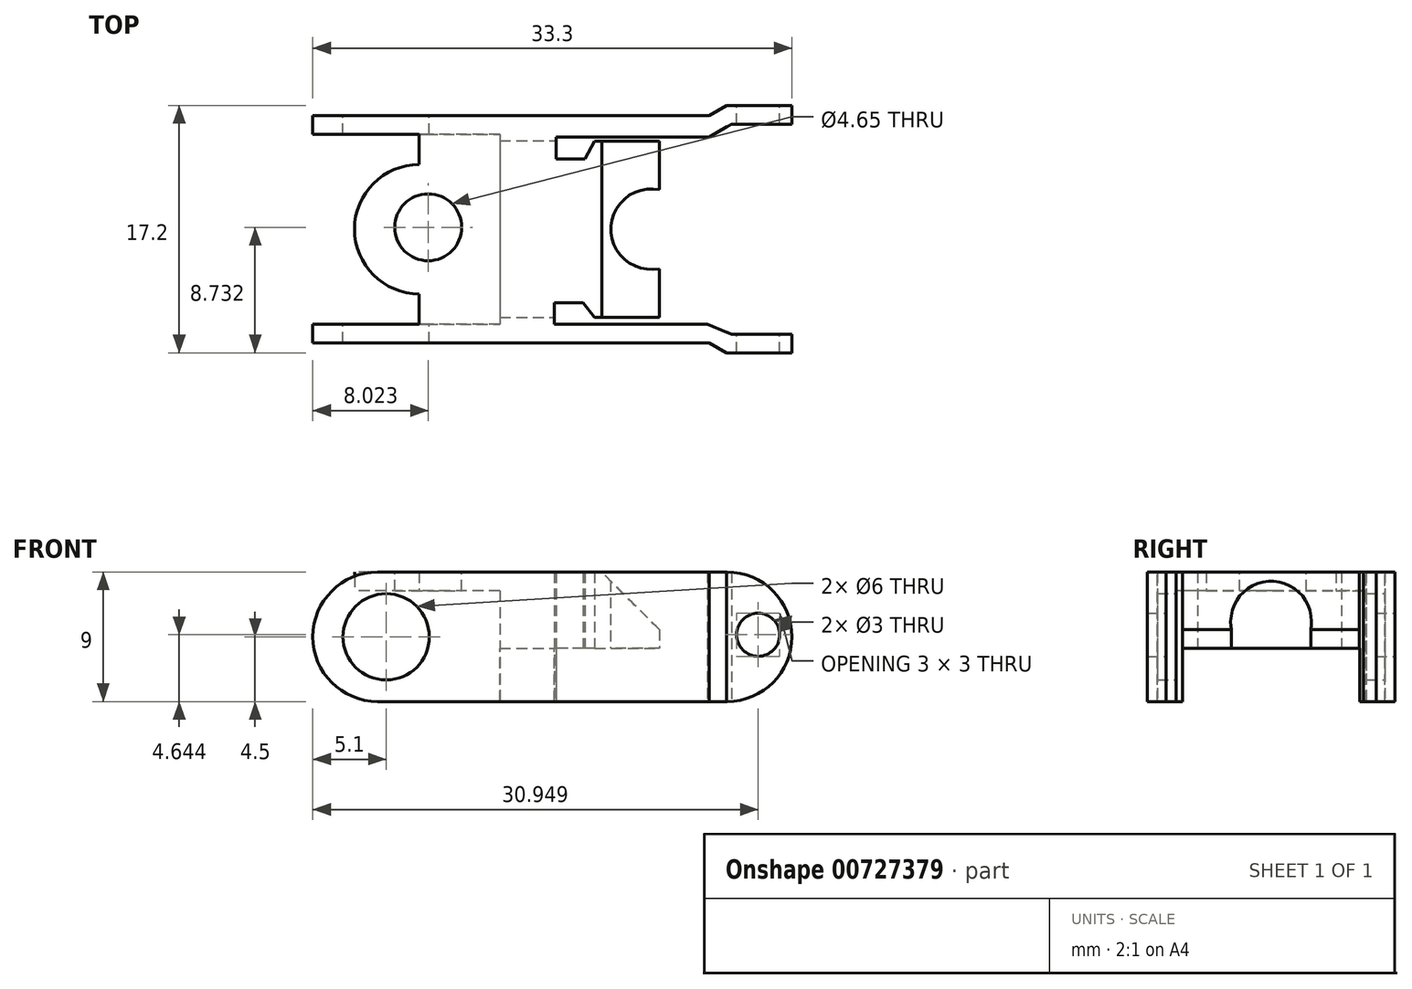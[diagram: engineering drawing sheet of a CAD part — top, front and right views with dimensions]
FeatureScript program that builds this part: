
annotation { "Feature Type Name" : "Feature", "Feature Type Description" : "" }
export const myFeature = defineFeature(function(context is Context, id is Id, definition is map)
    precondition{}
    {
        {
            var Q0;
            Q0=qCreatedBy(makeId("Top.planeOp"),FACE);
            var sketch = newSketch(context, id + "F0", { "sketchPlane" : qUnion([Q0])});
            skLineSegment(sketch, "E0", {"start": v(0, 0) * mm, "end": v(0, 1.3) * mm});
            skLineSegment(sketch, "E1", {"start": v(0, 1.3) * mm, "end": v(7.4, 1.3) * mm});
            skLineSegment(sketch, "E2", {"start": v(7.4, 1.3) * mm, "end": v(7.4, 3.4) * mm});
            skArc(sketch, "E3", {"start": v(7.4, 12.4) * mm, "mid": v(2.9, 7.9) * mm, "end": v(7.4, 3.4) * mm});
            skLineSegment(sketch, "E4", {"start": v(0, 0) * mm, "end": v(27.53, 0) * mm});
            skLineSegment(sketch, "E5", {"start": v(16.8, 1.3) * mm, "end": v(16.8, 2.8) * mm});
            skLineSegment(sketch, "E6", {"start": v(16.8, 2.8) * mm, "end": v(18.8, 2.8) * mm});
            skLineSegment(sketch, "E7", {"start": v(18.8, 2.8) * mm, "end": v(19.58, 1.76) * mm});
            skLineSegment(sketch, "E8", {"start": v(19.58, 1.76) * mm, "end": v(24.08, 1.76) * mm});
            skLineSegment(sketch, "E9", {"start": v(24.08, 1.76) * mm, "end": v(24.08, 5.15) * mm});
            skLineSegment(sketch, "E10", {"start": v(27.43, 1.3) * mm, "end": v(16.8, 1.3) * mm});
            skLineSegment(sketch, "E11.MirrorCS", {"start": v(7.4, 14.5) * mm, "end": v(7.4, 12.4) * mm});
            skLineSegment(sketch, "E12.MirrorCS", {"start": v(0, 14.5) * mm, "end": v(7.4, 14.5) * mm});
            skLineSegment(sketch, "E13.MirrorCS", {"start": v(0, 15.8) * mm, "end": v(0, 14.5) * mm});
            skLineSegment(sketch, "E14.MirrorCS", {"start": v(0, 15.8) * mm, "end": v(27.53, 15.8) * mm});
            skLineSegment(sketch, "E15.MirrorCS", {"start": v(16.9, 12.8) * mm, "end": v(18.9, 12.8) * mm});
            skLineSegment(sketch, "E16.MirrorCS", {"start": v(16.9, 14.3) * mm, "end": v(16.9, 12.8) * mm});
            skLineSegment(sketch, "E17.MirrorCS", {"start": v(27.53, 14.3) * mm, "end": v(16.9, 14.3) * mm});
            skLineSegment(sketch, "E18.MirrorCS", {"start": v(24.08, 14.04) * mm, "end": v(24.08, 10.65) * mm});
            skPoint(sketch, "E19.end.orphan", {"position": v(27.53, 0) * mm});
            skPoint(sketch, "E20.trimOffspring.end.orphan", {"position": v(37.89, 7.9) * mm});
            skLineSegment(sketch, "E21", {"start": v(7.4, 7.9) * mm, "end": v(37.89, 7.9) * mm, "construction": true});
            skLineSegment(sketch, "E22", {"start": v(7.4, 3.4) * mm, "end": v(7.4, 12.4) * mm, "construction": true});
            skPoint(sketch, "E23.orphan", {"position": v(0, 15.8) * mm});
            skLineSegment(sketch, "E24", {"start": v(27.53, 15.8) * mm, "end": v(27.53, 13.9) * mm, "construction": true});
            skLineSegment(sketch, "E25", {"start": v(27.53, 15.8) * mm, "end": v(28.75, 16.5) * mm});
            skLineSegment(sketch, "E26", {"start": v(28.75, 16.5) * mm, "end": v(33.3, 16.5) * mm});
            skLineSegment(sketch, "E27", {"start": v(33.3, 16.5) * mm, "end": v(33.3, 15.2) * mm});
            skLineSegment(sketch, "E28", {"start": v(33.3, 15.2) * mm, "end": v(29.1, 15.2) * mm});
            skLineSegment(sketch, "E29", {"start": v(29.1, 15.2) * mm, "end": v(27.53, 14.3) * mm});
            skLineSegment(sketch, "E30.MirrorCS", {"start": v(28.75, -0.7) * mm, "end": v(33.3, -0.7) * mm});
            skLineSegment(sketch, "E31.MirrorCS", {"start": v(33.3, 0.6) * mm, "end": v(29.1, 0.6) * mm});
            skLineSegment(sketch, "E32.MirrorCS", {"start": v(33.3, -0.7) * mm, "end": v(33.3, 0.6) * mm});
            skLineSegment(sketch, "E33.MirrorCS", {"start": v(27.53, 0) * mm, "end": v(28.75, -0.7) * mm});
            skLineSegment(sketch, "E34", {"start": v(27.43, 1.3) * mm, "end": v(29.1, 0.6) * mm});
            skLineSegment(sketch, "E35.MirrorCS", {"start": v(19.58, 14.04) * mm, "end": v(24.08, 14.04) * mm});
            skLineSegment(sketch, "E36", {"start": v(18.9, 12.8) * mm, "end": v(19.58, 14.04) * mm});
            skArc(sketch, "E37", {"start": v(24.08, 10.65) * mm, "mid": v(20.7, 7.9) * mm, "end": v(24.08, 5.15) * mm});
            skSolve(sketch);
        }
        {
            var Q0;
            Q0=qSketchRegion(id+"F0",true);
            extrude(context, id + "F1", {"entities" : qUnion([Q0]), "depth" : 9 * mm, "offsetDistance" : 25 * mm});
        }
        {
            var Q0;
            Q0=makeQuery(id+"F1.opExtrude","SWEPT_FACE",FACE,{"disambiguationData":[OSD([sQuery(id+"F0.wireOp",EDGE,"E0")])]});
            var sketch = newSketch(context, id + "F2", { "sketchPlane" : qUnion([Q0])});
            skLineSegment(sketch, "E38.bottom", {"start": v(-14.5, 7.7) * mm, "end": v(-1.3, 7.7) * mm});
            skLineSegment(sketch, "E38.top", {"start": v(-14.5, 0) * mm, "end": v(-1.3, 0) * mm});
            skLineSegment(sketch, "E38.left", {"start": v(-14.5, 7.7) * mm, "end": v(-14.5, 0) * mm});
            skLineSegment(sketch, "E38.right", {"start": v(-1.3, 7.7) * mm, "end": v(-1.3, 0) * mm});
            skSolve(sketch);
        }
        {
            var Q0;
            Q0=qSketchRegion(id+"F2",true);
            extrude(context, id + "F3", {"entities" : qUnion([Q0]), "operationType" : NewBodyOperationType.REMOVE, "oppositeDirection" : true, "depth" : 13 * mm, "offsetDistance" : 25 * mm});
        }
        {
            var Q0;
            Q0=makeQuery(id+"F1.opExtrude","CAP_EDGE",EDGE,{"disambiguationData":[OSD([sQuery(id+"F0.wireOp",EDGE,"E9")])],"isStart":false});
            var Q1;
            Q1=makeQuery(id+"F1.opExtrude","CAP_EDGE",EDGE,{"disambiguationData":[OSD([sQuery(id+"F0.wireOp",EDGE,"E18.MirrorCS")])],"isStart":false});
            chamfer(context, id + "F4", {"entities" : qUnion([Q0, Q1]), "width" : 4 * mm, "tangentPropagation" : true});
        }
        {
            var Q0;
            Q0=makeQuery(id+"F1.opExtrude","CAP_EDGE",EDGE,{"disambiguationData":[OSD([sQuery(id+"F0.wireOp",EDGE,"E32.MirrorCS")])],"isStart":true});
            var Q1;
            Q1=makeQuery(id+"F1.opExtrude","CAP_EDGE",EDGE,{"disambiguationData":[OSD([sQuery(id+"F0.wireOp",EDGE,"E32.MirrorCS")])],"isStart":false});
            var Q2;
            Q2=makeQuery(id+"F1.opExtrude","CAP_EDGE",EDGE,{"disambiguationData":[OSD([sQuery(id+"F0.wireOp",EDGE,"E27")])],"isStart":true});
            var Q3;
            Q3=makeQuery(id+"F1.opExtrude","CAP_EDGE",EDGE,{"disambiguationData":[OSD([sQuery(id+"F0.wireOp",EDGE,"E27")])],"isStart":false});
            var Q4;
            Q4=makeQuery(id+"F1.opExtrude","CAP_EDGE",EDGE,{"disambiguationData":[OSD([sQuery(id+"F0.wireOp",EDGE,"E13.MirrorCS")])],"isStart":true});
            var Q5;
            Q5=makeQuery(id+"F1.opExtrude","CAP_EDGE",EDGE,{"disambiguationData":[OSD([sQuery(id+"F0.wireOp",EDGE,"E13.MirrorCS")])],"isStart":false});
            var Q6;
            Q6=makeQuery(id+"F1.opExtrude","CAP_EDGE",EDGE,{"disambiguationData":[OSD([sQuery(id+"F0.wireOp",EDGE,"E0")])],"isStart":true});
            var Q7;
            Q7=makeQuery(id+"F1.opExtrude","CAP_EDGE",EDGE,{"disambiguationData":[OSD([sQuery(id+"F0.wireOp",EDGE,"E0")])],"isStart":false});
            fillet(context, id + "F5", {"entities" : qUnion([Q0, Q1, Q2, Q3, Q4, Q5, Q6, Q7]), "radius" : 4.5 * mm, "tangentPropagation" : true, "allowEdgeOverflow" : false});
        }
        {
            var Q0;
            Q0=makeQuery(id+"F1.opExtrude","SWEPT_FACE",FACE,{"disambiguationData":[OSD([sQuery(id+"F0.wireOp",EDGE,"E14.MirrorCS")])]});
            var sketch = newSketch(context, id + "F6", { "sketchPlane" : qUnion([Q0])});
            skCircle(sketch, "E39", {"center": v(-5.1, 4.5) * mm, "radius": 3 * mm});
            skSolve(sketch);
        }
        {
            var Q0;
            Q0=makeQuery(id+"F1.opExtrude","CAP_FACE",FACE,{"disambiguationData":[OSD([sQuery(id+"F0.wireOp",EDGE,"E0"),sQuery(id+"F0.wireOp",EDGE,"E1"),sQuery(id+"F0.wireOp",EDGE,"E2"),sQuery(id+"F0.wireOp",EDGE,"E3"),sQuery(id+"F0.wireOp",EDGE,"E4"),sQuery(id+"F0.wireOp",EDGE,"E5"),sQuery(id+"F0.wireOp",EDGE,"E6"),sQuery(id+"F0.wireOp",EDGE,"E7"),sQuery(id+"F0.wireOp",EDGE,"E8"),sQuery(id+"F0.wireOp",EDGE,"E9"),sQuery(id+"F0.wireOp",EDGE,"E10"),sQuery(id+"F0.wireOp",EDGE,"E11.MirrorCS"),sQuery(id+"F0.wireOp",EDGE,"E12.MirrorCS"),sQuery(id+"F0.wireOp",EDGE,"E13.MirrorCS"),sQuery(id+"F0.wireOp",EDGE,"E15.MirrorCS"),sQuery(id+"F0.wireOp",EDGE,"E16.MirrorCS"),sQuery(id+"F0.wireOp",EDGE,"E17.MirrorCS"),sQuery(id+"F0.wireOp",EDGE,"13fdda64-d4ae-4b14-ad6a-07e018b78b787.MirrorCS"),sQuery(id+"F0.wireOp",EDGE,"13fdda64-d4ae-4b14-ad6a-07e018b78b788.MirrorCS"),sQuery(id+"F0.wireOp",EDGE,"E14.MirrorCS"),sQuery(id+"F0.wireOp",EDGE,"E18.MirrorCS"),sQuery(id+"F0.wireOp",EDGE,"QRLhJHuq-ugKA-eGBM-L1QN-SyeUm9ubxrph"),sQuery(id+"F0.wireOp",EDGE,"E25"),sQuery(id+"F0.wireOp",EDGE,"E26"),sQuery(id+"F0.wireOp",EDGE,"E27"),sQuery(id+"F0.wireOp",EDGE,"E28"),sQuery(id+"F0.wireOp",EDGE,"E29"),sQuery(id+"F0.wireOp",EDGE,"E30.MirrorCS"),sQuery(id+"F0.wireOp",EDGE,"E31.MirrorCS"),sQuery(id+"F0.wireOp",EDGE,"E32.MirrorCS"),sQuery(id+"F0.wireOp",EDGE,"E33.MirrorCS"),sQuery(id+"F0.wireOp",EDGE,"E34")])],"isStart":false});
            var sketch = newSketch(context, id + "F7", { "sketchPlane" : qUnion([Q0])});
            skCircle(sketch, "E40", {"center": v(8.02, 8.03) * mm, "radius": 2.33 * mm});
            skSolve(sketch);
        }
        {
            var Q0;
            Q0=qSketchRegion(id+"F7",true);
            extrude(context, id + "F8", {"entities" : qUnion([Q0]), "operationType" : NewBodyOperationType.REMOVE, "endBound" : BoundingType.THROUGH_ALL, "oppositeDirection" : true, "depth" : 25 * mm, "offsetDistance" : 25 * mm});
        }
        {
            var Q0;
            Q0=makeQuery(id+"F4.opChamfer","BLEND_FACE",FACE,{"disambiguationData":[OSD([sQuery(id+"F0.wireOp",EDGE,"E9")])]});
            cPlane(context, id + "F9", {"entities" : qUnion([Q0]), "cplaneType" : CPlaneType.OFFSET, "offset" : 1.3 * mm, "oppositeDirection" : true, "width" : 150 * mm, "height" : 150 * mm});
        }
        {
            var Q0;
            Q0=qSketchRegion(id+"F6",true);
            extrude(context, id + "F10", {"entities" : qUnion([Q0]), "operationType" : NewBodyOperationType.REMOVE, "endBound" : BoundingType.THROUGH_ALL, "oppositeDirection" : true, "depth" : 25 * mm, "offsetDistance" : 25 * mm});
        }
        {
            var Q0;
            Q0=makeQuery(id+"F1.opExtrude","SWEPT_FACE",FACE,{"disambiguationData":[OSD([sQuery(id+"F0.wireOp",EDGE,"E9")])]});
            var sketch = newSketch(context, id + "F11", { "sketchPlane" : qUnion([Q0])});
            skLineSegment(sketch, "E41.bottom", {"start": v(1.76, 3.7) * mm, "end": v(14.05, 3.7) * mm});
            skLineSegment(sketch, "E41.top", {"start": v(1.76, 0) * mm, "end": v(14.05, 0) * mm});
            skLineSegment(sketch, "E41.left", {"start": v(1.76, 3.7) * mm, "end": v(1.76, 0) * mm});
            skLineSegment(sketch, "E41.right", {"start": v(14.05, 3.7) * mm, "end": v(14.05, 0) * mm});
            skSolve(sketch);
        }
        {
            var Q0;
            Q0=qSketchRegion(id+"F11",true);
            extrude(context, id + "F12", {"entities" : qUnion([Q0]), "operationType" : NewBodyOperationType.REMOVE, "endBound" : BoundingType.THROUGH_ALL, "oppositeDirection" : true, "depth" : 25 * mm, "offsetDistance" : 25 * mm});
        }
        {
            var Q0;
            Q0=makeQuery(id+"F1.opExtrude","SWEPT_FACE",FACE,{"disambiguationData":[OSD([sQuery(id+"F0.wireOp",EDGE,"E26")])]});
            var sketch = newSketch(context, id + "F13", { "sketchPlane" : qUnion([Q0])});
            skCircle(sketch, "E42", {"center": v(-30.95, 4.64) * mm, "radius": 1.5 * mm});
            skSolve(sketch);
        }
        {
            var Q0;
            Q0=qSketchRegion(id+"F13",true);
            extrude(context, id + "F14", {"entities" : qUnion([Q0]), "operationType" : NewBodyOperationType.REMOVE, "endBound" : BoundingType.THROUGH_ALL, "oppositeDirection" : true, "depth" : 25 * mm, "offsetDistance" : 25 * mm});
        }
    });
